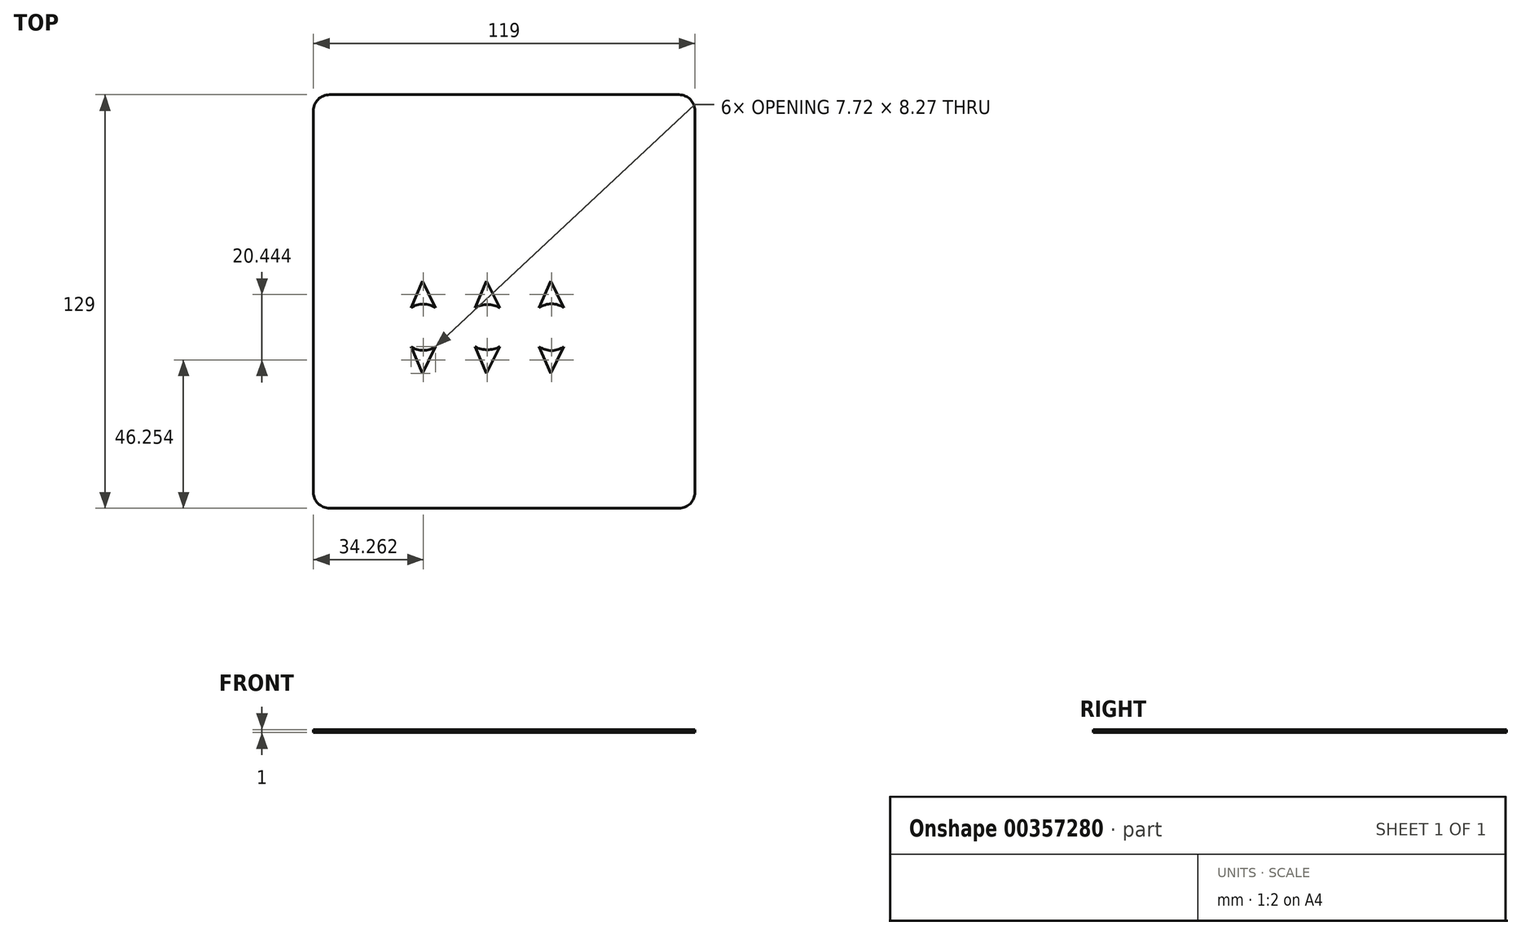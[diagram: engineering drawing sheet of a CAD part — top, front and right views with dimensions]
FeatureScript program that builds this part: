
annotation { "Feature Type Name" : "Feature", "Feature Type Description" : "" }
export const myFeature = defineFeature(function(context is Context, id is Id, definition is map)
    precondition{}
    {
        {
            var Q0;
            Q0=qCreatedBy(makeId("Top.planeOp"),FACE);
            var sketch = newSketch(context, id + "F0", { "sketchPlane" : qUnion([Q0])});
            skLineSegment(sketch, "E0.bottom", {"start": v(54, -65) * mm, "end": v(-55, -65) * mm});
            skLineSegment(sketch, "E0.top", {"start": v(54, 64) * mm, "end": v(-55, 64) * mm});
            skLineSegment(sketch, "E0.left", {"start": v(59, -60) * mm, "end": v(59, 59) * mm});
            skLineSegment(sketch, "E0.right", {"start": v(-60, -60) * mm, "end": v(-60, 59) * mm});
            skLineSegment(sketch, "E1", {"start": v(-26.04, 5.83) * mm, "end": v(-29.6, -2.44) * mm});
            skLineSegment(sketch, "E2", {"start": v(-26.04, 5.83) * mm, "end": v(-21.88, -2.44) * mm});
            skLineSegment(sketch, "E3", {"start": v(-9.6, -2.44) * mm, "end": v(-6.04, 5.83) * mm});
            skLineSegment(sketch, "E4", {"start": v(-6.04, 5.83) * mm, "end": v(-1.88, -2.44) * mm});
            skLineSegment(sketch, "E5", {"start": v(10.4, -2.44) * mm, "end": v(13.96, 5.83) * mm});
            skLineSegment(sketch, "E6", {"start": v(13.96, 5.83) * mm, "end": v(18.12, -2.44) * mm});
            skLineSegment(sketch, "E7", {"start": v(-29.6, -2.44) * mm, "end": v(22.11, -2.44) * mm, "construction": true});
            skArc(sketch, "E8", {"start": v(-21.88, -2.44) * mm, "mid": v(-25.74, -1.33) * mm, "end": v(-29.6, -2.44) * mm});
            skArc(sketch, "E9", {"start": v(-1.88, -2.44) * mm, "mid": v(-5.74, -1.48) * mm, "end": v(-9.6, -2.44) * mm});
            skArc(sketch, "E10", {"start": v(18.12, -2.44) * mm, "mid": v(14.26, -1.25) * mm, "end": v(10.4, -2.44) * mm});
            skLineSegment(sketch, "E11.MirrorCS", {"start": v(-9.6, -14.61) * mm, "end": v(-6.04, -22.88) * mm});
            skLineSegment(sketch, "E12.MirrorCS", {"start": v(-26.04, -22.88) * mm, "end": v(-21.88, -14.61) * mm});
            skLineSegment(sketch, "E13.MirrorCS", {"start": v(-6.04, -22.88) * mm, "end": v(-1.88, -14.61) * mm});
            skLineSegment(sketch, "E14.MirrorCS", {"start": v(-26.04, -22.88) * mm, "end": v(-29.6, -14.61) * mm});
            skLineSegment(sketch, "E15.MirrorCS", {"start": v(10.4, -14.61) * mm, "end": v(13.96, -22.88) * mm});
            skArc(sketch, "E16.MirrorCS", {"start": v(-21.88, -14.61) * mm, "mid": v(-25.74, -15.72) * mm, "end": v(-29.6, -14.61) * mm});
            skArc(sketch, "E17.MirrorCS", {"start": v(-1.88, -14.61) * mm, "mid": v(-5.74, -15.57) * mm, "end": v(-9.6, -14.61) * mm});
            skArc(sketch, "E18.MirrorCS", {"start": v(18.12, -14.61) * mm, "mid": v(14.26, -15.8) * mm, "end": v(10.4, -14.61) * mm});
            skLineSegment(sketch, "E19.MirrorCS", {"start": v(13.96, -22.88) * mm, "end": v(18.12, -14.61) * mm});
            skPoint(sketch, "E20.visualSharp", {"position": v(-60, 64) * mm});
            skArc(sketch, "E20.filletArc", {"start": v(-55, 64) * mm, "mid": v(-58.54, 62.54) * mm, "end": v(-60, 59) * mm});
            skPoint(sketch, "E21.visualSharp", {"position": v(59, 64) * mm});
            skArc(sketch, "E21.filletArc", {"start": v(59, 59) * mm, "mid": v(57.54, 62.54) * mm, "end": v(54, 64) * mm});
            skPoint(sketch, "E22.visualSharp", {"position": v(59, -65) * mm});
            skArc(sketch, "E22.filletArc", {"start": v(54, -65) * mm, "mid": v(57.54, -63.54) * mm, "end": v(59, -60) * mm});
            skPoint(sketch, "E23.visualSharp", {"position": v(-60, -65) * mm});
            skArc(sketch, "E23.filletArc", {"start": v(-60, -60) * mm, "mid": v(-58.54, -63.54) * mm, "end": v(-55, -65) * mm});
            skSolve(sketch);
        }
        {
            var Q0;
            Q0=makeQuery(id+"F0.imprint","IMPRINT",FACE,{"disambiguationData":[TD([[makeQuery(id+"F0.imprint","IMPRINT",EDGE,{"derivedFrom":sQuery(id+"F0.wireOp",EDGE,"E0.bottom")}),-1.0]])]});
            extrude(context, id + "F1", {"entities" : qUnion([Q0]), "depth" : 1 * mm});
        }
    });
